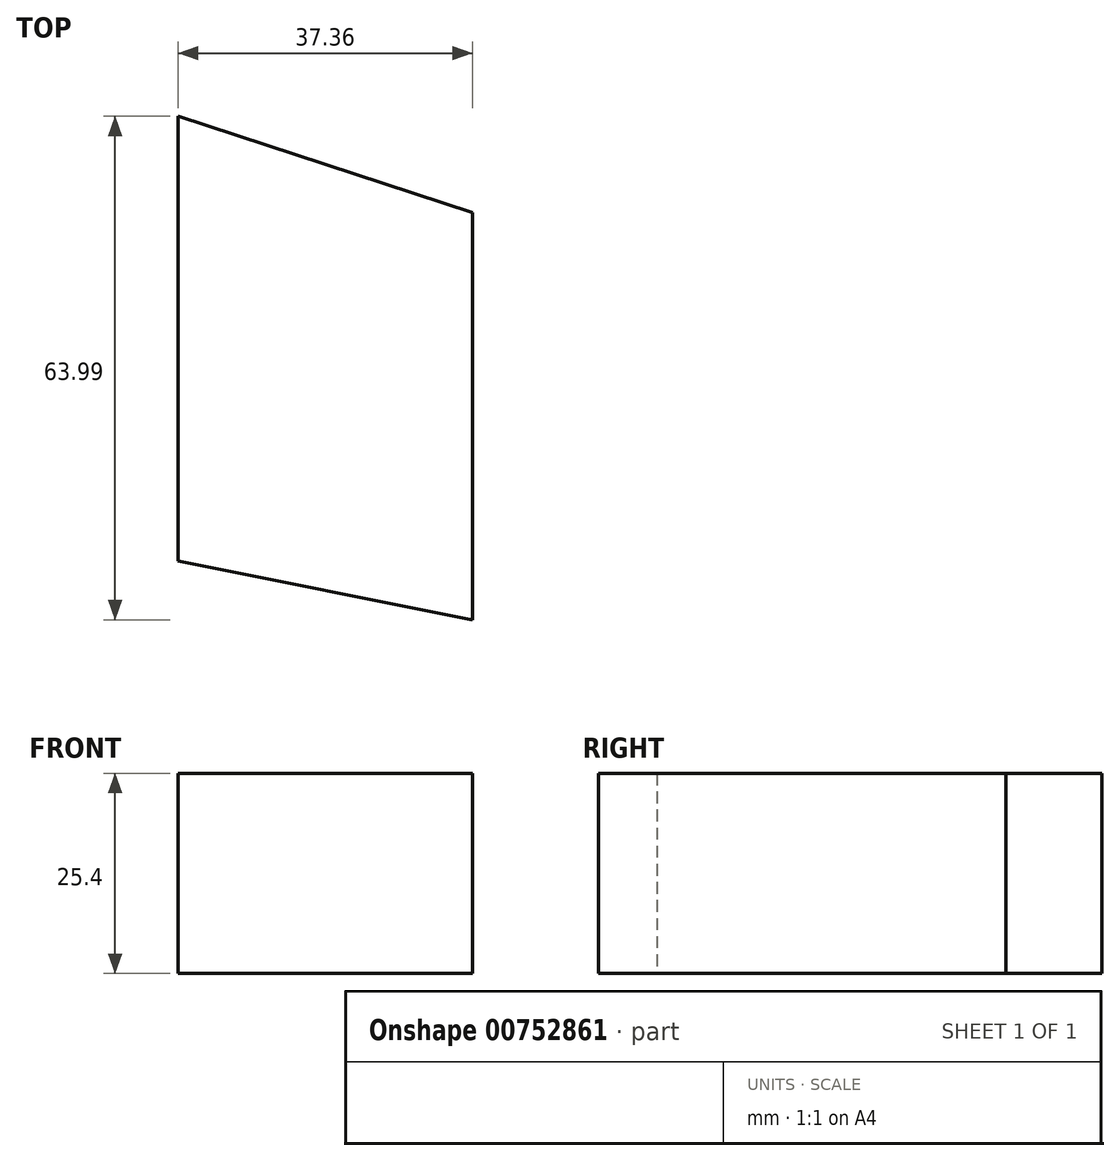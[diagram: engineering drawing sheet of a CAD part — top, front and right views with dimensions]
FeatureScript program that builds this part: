
annotation { "Feature Type Name" : "Feature", "Feature Type Description" : "" }
export const myFeature = defineFeature(function(context is Context, id is Id, definition is map)
    precondition{}
    {
        {
            var Q0;
            Q0=qCreatedBy(makeId("Top.planeOp"),FACE);
            var sketch = newSketch(context, id + "F0", { "sketchPlane" : qUnion([Q0])});
            skLineSegment(sketch, "E0", {"start": v(-8.34, 7.48) * mm, "end": v(-8.34, 64) * mm});
            skLineSegment(sketch, "E1", {"start": v(-8.34, 64) * mm, "end": v(29.02, 51.76) * mm});
            skLineSegment(sketch, "E2", {"start": v(29.02, 51.76) * mm, "end": v(29.02, 0) * mm});
            skLineSegment(sketch, "E3", {"start": v(29.02, 0) * mm, "end": v(-8.34, 7.48) * mm});
            skSolve(sketch);
        }
        {
            var Q0;
            Q0 = qSketchRegion(id + "F0", true);
            extrude(context, id + "F1", {"entities" : qUnion([Q0]), "depth" : 25.4 * mm, "offsetDistance" : 25.4 * mm});
        }
    });
